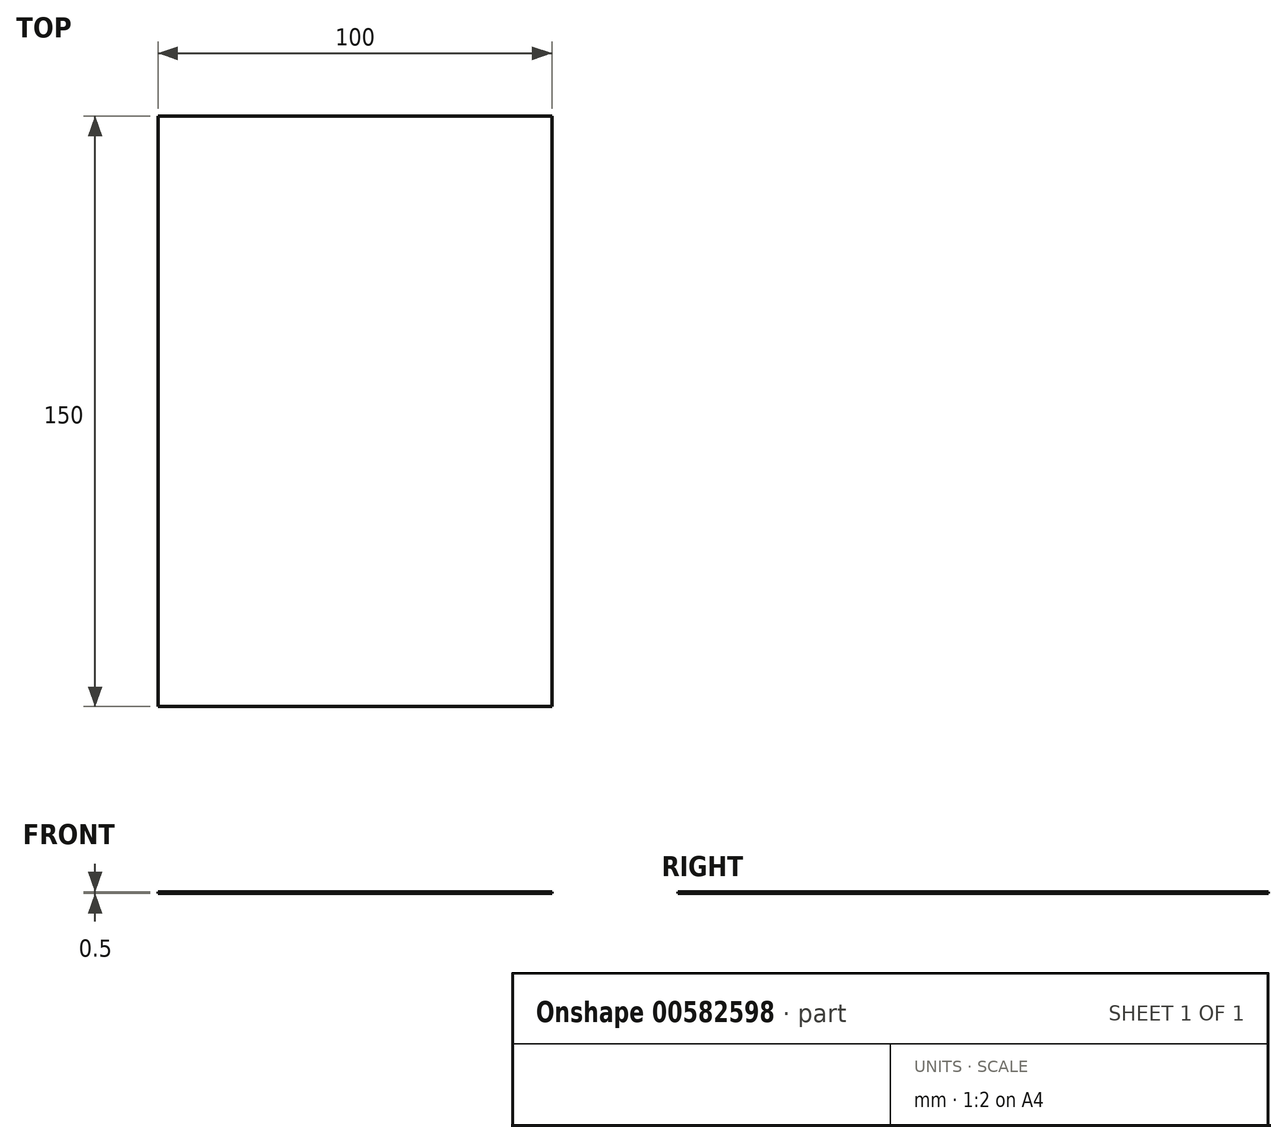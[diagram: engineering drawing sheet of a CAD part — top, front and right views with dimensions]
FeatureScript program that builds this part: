
annotation { "Feature Type Name" : "Feature", "Feature Type Description" : "" }
export const myFeature = defineFeature(function(context is Context, id is Id, definition is map)
    precondition{}
    {
        {
            var Q0;
            Q0=qCreatedBy(makeId("Top.planeOp"),FACE);
            var sketch = newSketch(context, id + "F0", { "sketchPlane" : qUnion([Q0])});
            skLineSegment(sketch, "E0.bottom", {"start": v(0, 0) * mm, "end": v(100, 0) * mm});
            skLineSegment(sketch, "E0.top", {"start": v(0, 150) * mm, "end": v(100, 150) * mm});
            skLineSegment(sketch, "E0.left", {"start": v(0, 0) * mm, "end": v(0, 150) * mm});
            skLineSegment(sketch, "E0.right", {"start": v(100, 0) * mm, "end": v(100, 150) * mm});
            skSolve(sketch);
        }
        {
            var Q0;
            Q0 = qSketchRegion(id + "F0", true);
            extrude(context, id + "F1", {"entities" : qUnion([Q0]), "depth" : 0.5 * mm, "offsetDistance" : 25 * mm});
        }
    });
